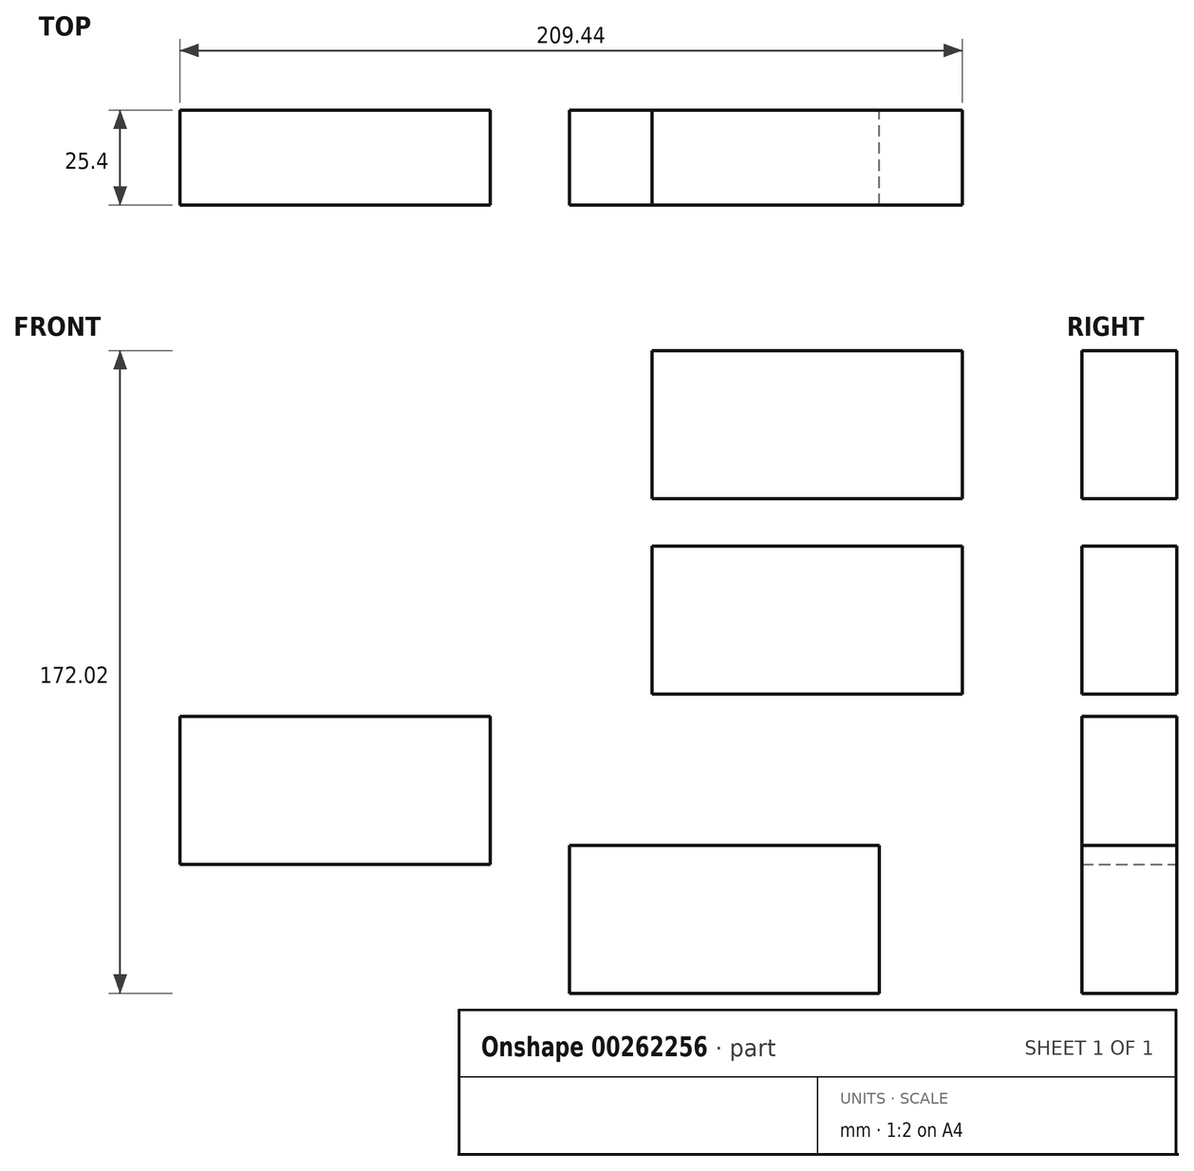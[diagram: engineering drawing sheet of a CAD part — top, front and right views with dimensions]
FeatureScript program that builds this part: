
annotation { "Feature Type Name" : "Feature", "Feature Type Description" : "" }
export const myFeature = defineFeature(function(context is Context, id is Id, definition is map)
    precondition{}
    {
        {
            var Q0;
            Q0=qCreatedBy(makeId("Front.planeOp"),FACE);
            var sketch = newSketch(context, id + "F0", { "sketchPlane" : qUnion([Q0])});
            skLineSegment(sketch, "E0.bottom", {"start": v(41.52, 19.8) * mm, "end": v(-41.52, 19.8) * mm});
            skLineSegment(sketch, "E0.top", {"start": v(41.52, -19.8) * mm, "end": v(-41.52, -19.8) * mm});
            skLineSegment(sketch, "E0.left", {"start": v(41.52, 19.8) * mm, "end": v(41.52, -19.8) * mm});
            skLineSegment(sketch, "E0.right", {"start": v(-41.52, 19.8) * mm, "end": v(-41.52, -19.8) * mm});
            skPoint(sketch, "E0.middle", {"position": v(0, 0) * mm});
            skLineSegment(sketch, "E1.bottom", {"start": v(41.52, 72.07) * mm, "end": v(-41.52, 72.07) * mm});
            skLineSegment(sketch, "E1.top", {"start": v(41.52, 32.45) * mm, "end": v(-41.52, 32.45) * mm});
            skLineSegment(sketch, "E1.left", {"start": v(41.52, 72.07) * mm, "end": v(41.52, 32.45) * mm});
            skLineSegment(sketch, "E1.right", {"start": v(-41.52, 72.07) * mm, "end": v(-41.52, 32.45) * mm});
            skPoint(sketch, "E1.middle", {"position": v(0, 52.26) * mm});
            skLineSegment(sketch, "E2.bottom", {"start": v(19.35, -60.34) * mm, "end": v(-63.68, -60.34) * mm});
            skLineSegment(sketch, "E2.top", {"start": v(19.35, -99.95) * mm, "end": v(-63.68, -99.95) * mm});
            skLineSegment(sketch, "E2.left", {"start": v(19.35, -60.34) * mm, "end": v(19.35, -99.95) * mm});
            skLineSegment(sketch, "E2.right", {"start": v(-63.68, -60.34) * mm, "end": v(-63.68, -99.95) * mm});
            skPoint(sketch, "E2.middle", {"position": v(-22.17, -80.14) * mm});
            skLineSegment(sketch, "E3.bottom", {"start": v(-84.88, -25.78) * mm, "end": v(-167.92, -25.78) * mm});
            skLineSegment(sketch, "E3.top", {"start": v(-84.88, -65.4) * mm, "end": v(-167.92, -65.4) * mm});
            skLineSegment(sketch, "E3.left", {"start": v(-84.88, -25.78) * mm, "end": v(-84.88, -65.4) * mm});
            skLineSegment(sketch, "E3.right", {"start": v(-167.92, -25.78) * mm, "end": v(-167.92, -65.4) * mm});
            skPoint(sketch, "E3.middle", {"position": v(-126.4, -45.6) * mm});
            skSolve(sketch);
        }
        {
            var Q0;
            Q0 = qSketchRegion(id + "F0", true);
            extrude(context, id + "F1", {"entities" : qUnion([Q0]), "depth" : 25.4 * mm});
        }
    });
